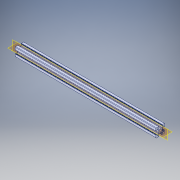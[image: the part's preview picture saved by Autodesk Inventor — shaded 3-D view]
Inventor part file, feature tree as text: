
AUTODESK INVENTOR PART (.ipt)
format: ipt  version: 2018 (Build 220112000, 112)  size: 370,688 bytes
history: native  units: in
note: dims shown in document units (in); Inventor stores cm internally (conversion verified against a paired STEP export)
features: extrude x1, sketch x1, projected_geometry x1, fillet x1
ambient origin geometry x8: Origin, YZ Plane, XZ Plane, XY Plane, X Axis, Y Axis, Z Axis, Center Point
bodies: Solid1 (feature_tree)
feature tree (4):
  extrude  "Extrusion2"  [1 undecoded]
  sketch  "Sketch3"  dims[d2=8.6614in d3=0.0in]
  projected_geometry  "Projected Loop2"
  fillet  "Fillet5"  [1 undecoded]
note: 2 required parameter values undecoded (feature->parameter linkage not recoverable at this tier; creation-order binding heuristic only, values carry confidence <= 0.55)
